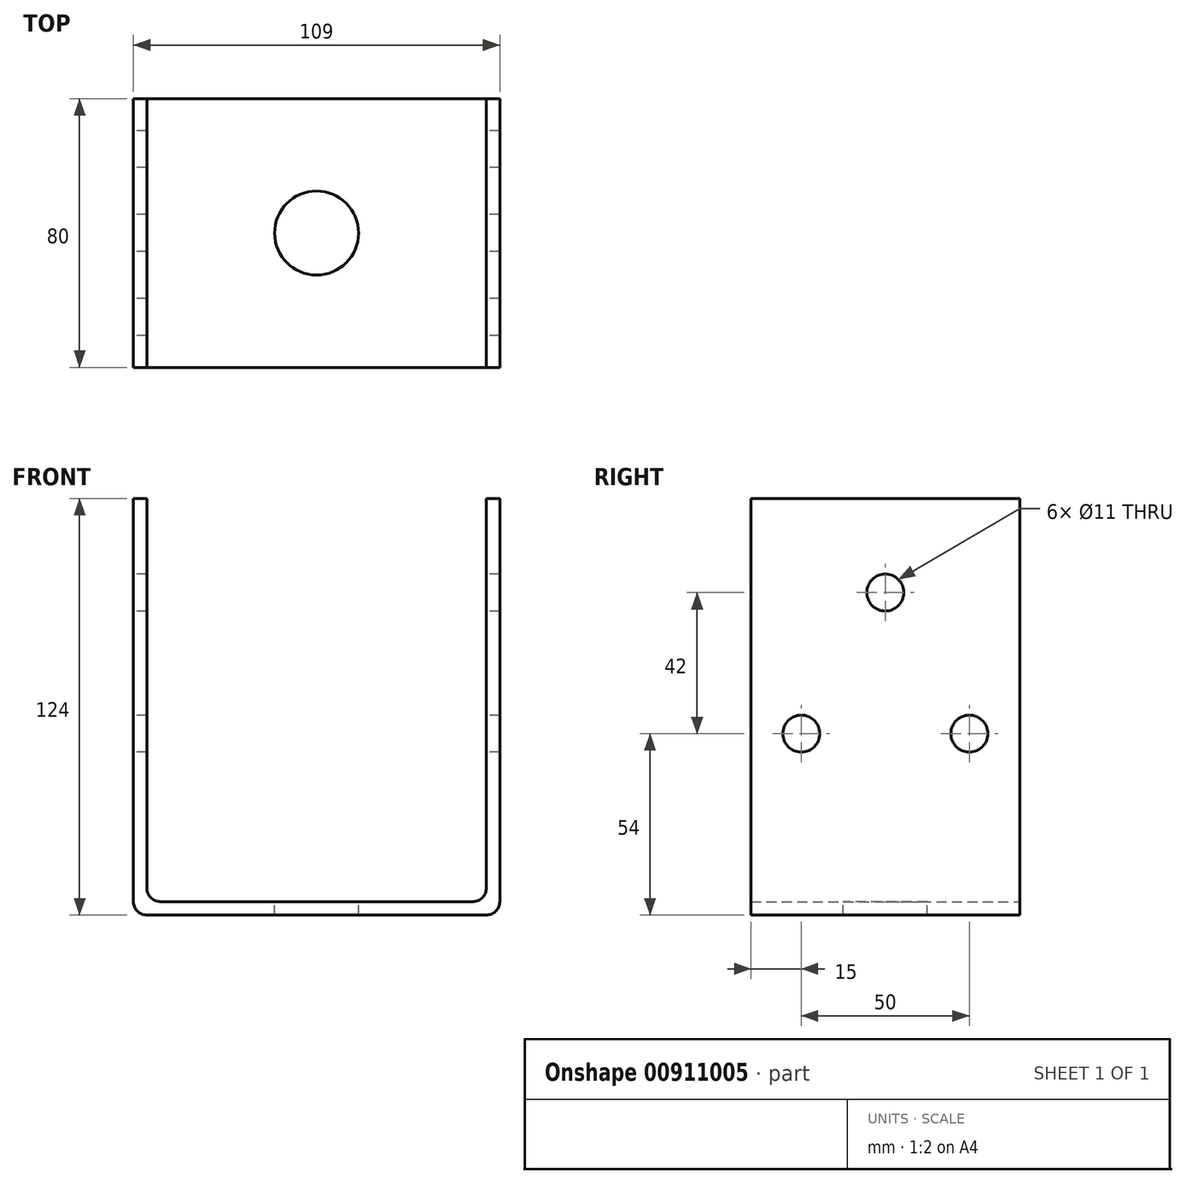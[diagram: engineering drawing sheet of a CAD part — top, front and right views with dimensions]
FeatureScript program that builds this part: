
annotation { "Feature Type Name" : "Feature", "Feature Type Description" : "" }
export const myFeature = defineFeature(function(context is Context, id is Id, definition is map)
    precondition{}
    {
        {
            var Q0;
            Q0=qCreatedBy(makeId("Front.planeOp"),FACE);
            var sketch = newSketch(context, id + "F0", { "sketchPlane" : qUnion([Q0])});
            skLineSegment(sketch, "E0", {"start": v(0, 120) * mm, "end": v(0, 0) * mm});
            skLineSegment(sketch, "E1", {"start": v(0, 0) * mm, "end": v(101, 0) * mm});
            skLineSegment(sketch, "E2", {"start": v(101, 0) * mm, "end": v(101, 120) * mm});
            skLineSegment(sketch, "E3.0", {"start": v(105, -4) * mm, "end": v(105, 120) * mm});
            skLineSegment(sketch, "E3.1", {"start": v(-4, -4) * mm, "end": v(105, -4) * mm});
            skLineSegment(sketch, "E3.2", {"start": v(-4, 120) * mm, "end": v(-4, -4) * mm});
            skLineSegment(sketch, "E4", {"start": v(-4, 120) * mm, "end": v(0, 120) * mm});
            skLineSegment(sketch, "E5", {"start": v(101, 120) * mm, "end": v(105, 120) * mm});
            skSolve(sketch);
        }
        {
            var Q0;
            Q0=makeQuery(id+"F0.imprint","IMPRINT",FACE,{"disambiguationData":[TD([[makeQuery(id+"F0.imprint","IMPRINT",EDGE,{"derivedFrom":sQuery(id+"F0.wireOp",EDGE,"E0")}),-1.0]])]});
            extrude(context, id + "F1", {"entities" : qUnion([Q0]), "depth" : 80 * mm, "offsetDistance" : 25 * mm});
        }
        {
            var Q0;
            Q0=makeQuery(id+"F1.opExtrude","SWEPT_FACE",FACE,{"disambiguationData":[OSD([sQuery(id+"F0.wireOp",EDGE,"E1")])]});
            var sketch = newSketch(context, id + "F2", { "sketchPlane" : qUnion([Q0])});
            skLineSegment(sketch, "E6", {"start": v(50.5, -80) * mm, "end": v(50.5, 0) * mm, "construction": true});
            skCircle(sketch, "E7", {"center": v(50.5, -40) * mm, "radius": 12.5 * mm});
            skSolve(sketch);
        }
        {
            var Q0;
            Q0=makeQuery(id+"F2.imprint","IMPRINT",FACE,{"disambiguationData":[TD([[makeQuery(id+"F2.imprint","IMPRINT",EDGE,{"derivedFrom":sQuery(id+"F2.wireOp",EDGE,"E7")}),1.0]])]});
            extrude(context, id + "F3", {"entities" : qUnion([Q0]), "operationType" : NewBodyOperationType.REMOVE, "endBound" : BoundingType.THROUGH_ALL, "oppositeDirection" : true, "depth" : 25 * mm, "offsetDistance" : 25 * mm});
        }
        {
            var Q0;
            Q0=makeQuery(id+"F1.opExtrude","SWEPT_FACE",FACE,{"disambiguationData":[OSD([sQuery(id+"F0.wireOp",EDGE,"E3.2")])]});
            var sketch = newSketch(context, id + "F4", { "sketchPlane" : qUnion([Q0])});
            skCircle(sketch, "E8", {"center": v(65, 50) * mm, "radius": 5.5 * mm});
            skLineSegment(sketch, "E9", {"start": v(40, 120) * mm, "end": v(40, 46.17) * mm, "construction": true});
            skCircle(sketch, "E10", {"center": v(40, 92) * mm, "radius": 5.5 * mm});
            skCircle(sketch, "E11.MirrorC", {"center": v(15, 50) * mm, "radius": 5.5 * mm});
            skSolve(sketch);
        }
        {
            var Q0;
            Q0 = qSketchRegion(id + "F4", true);
            extrude(context, id + "F5", {"entities" : qUnion([Q0]), "operationType" : NewBodyOperationType.REMOVE, "endBound" : BoundingType.THROUGH_ALL, "oppositeDirection" : true, "depth" : 25 * mm, "offsetDistance" : 25 * mm});
        }
        {
            var Q0;
            Q0=makeQuery(id+"F1.opExtrude","SWEPT_EDGE",EDGE,{"disambiguationData":[OSD([sQuery(id+"F0.wireOp",EDGE,"E0"),sQuery(id+"F0.wireOp",EDGE,"E1")])]});
            var Q1;
            Q1=makeQuery(id+"F1.opExtrude","SWEPT_EDGE",EDGE,{"disambiguationData":[OSD([sQuery(id+"F0.wireOp",EDGE,"E1"),sQuery(id+"F0.wireOp",EDGE,"E2")])]});
            var Q2;
            Q2=makeQuery(id+"F1.opExtrude","SWEPT_EDGE",EDGE,{"disambiguationData":[OSD([sQuery(id+"F0.wireOp",EDGE,"E3.1"),sQuery(id+"F0.wireOp",EDGE,"E3.2")])]});
            var Q3;
            Q3=makeQuery(id+"F1.opExtrude","SWEPT_EDGE",EDGE,{"disambiguationData":[OSD([sQuery(id+"F0.wireOp",EDGE,"E3.0"),sQuery(id+"F0.wireOp",EDGE,"E3.1")])]});
            fillet(context, id + "F6", {"entities" : qUnion([Q0, Q1, Q2, Q3]), "radius" : 4 * mm, "tangentPropagation" : true, "allowEdgeOverflow" : false});
        }
    });
